# Revit family: PRD_AR_WstBns_RODANLidForWasteBin_RODX608
name_source: partatom
category: Specialty Equipment
revit_build: Autodesk Revit 2018 (Build: 20190510_1515(x64)
units: mm (PartAtom-declared; Revit-internal decimal feet)

## family parameters
Always vertical = Yes
Cut with Voids When Loaded = No
OmniClass Number = 23.40.20.31
OmniClass Title = Refuse Disposal Furniture
Part Type = Normal
Room Calculation Point = No
Round Connector Dimension = Use Diameter
Shared = No
Work Plane-Based = No

## types (1)
- RODX608
    AssetType = Fixed
    BIMObjectName = PRD_AR_WasteBins_RODANLidForWasteBin_RODX608
    Category = Pr_40_50_07_96, Waste bins
    Description = Folding self-closing lid for waste bin RODX607, stainless steel, surface satin finished, material thickness 0.8 mm, cylinder lock with KWC standard key, without waste bin.
    DurationUnit = year
    Features = stainless steel, surface satin finished
    Finish = satin finished
    GrossWeight = 3.93 kg
    IfcExportAs = IfcFurnitureType
    IfcExportType = USERDEFINED
    IsBuiltIn = TRUE
    Lock = Key-lock
    MainColor = stainless steel
    Manufacturer = KWC Group AG
    ManufacturerName = KWC Group AG
    ManufacturerURL = www.kwc.com
    Material = stainless steel
    MaterialCode = 1.4301
    MaterialThickness = 0.80 mm
    Model = RODX608
    ModelNumber = 2000101357
    ModelReference = RODX608
    NBSDescription = Waste bins
    NBSReference = 45-35-72/380
    Name = Folding Self-Closing Lid For Waste Bin RODX608
    NetWeight = 3.32 kg
    NominalDepth = 210 mm  [stored 0.688976 ft]
    NominalHeight = 192 mm  [stored 0.629921 ft]
    NominalWidth = 480 mm  [stored 1.5748 ft]
    ProductInformation = https://pim.kwc.com
    Size = 210 x 192 x 480 mm
    SlotHeight = 120.00 mm
    SlotWidth = 350.00 mm
    TypeOfFixing = Catch
    TypeOfMounting = On waste bin
    URL = www.kwc.com
    Uniclass2015Code = Pr_40_50_07_96
    Uniclass2015Title = Waste bins
    Uniclass2015Version = Products v1.10
    Version = 1
    WarrantyDurationUnit = year
    WasteBinMaterial = PRD_AR_StainlessSteel_SatinFinished_Perforated

note: [stored X ft] marks values corroborated as IEEE doubles in the binary element streams (Revit-internal decimal feet)

## geometry (parser evidence)
native form markers: Sweep x2
no freeform markers — native parametric forms only
